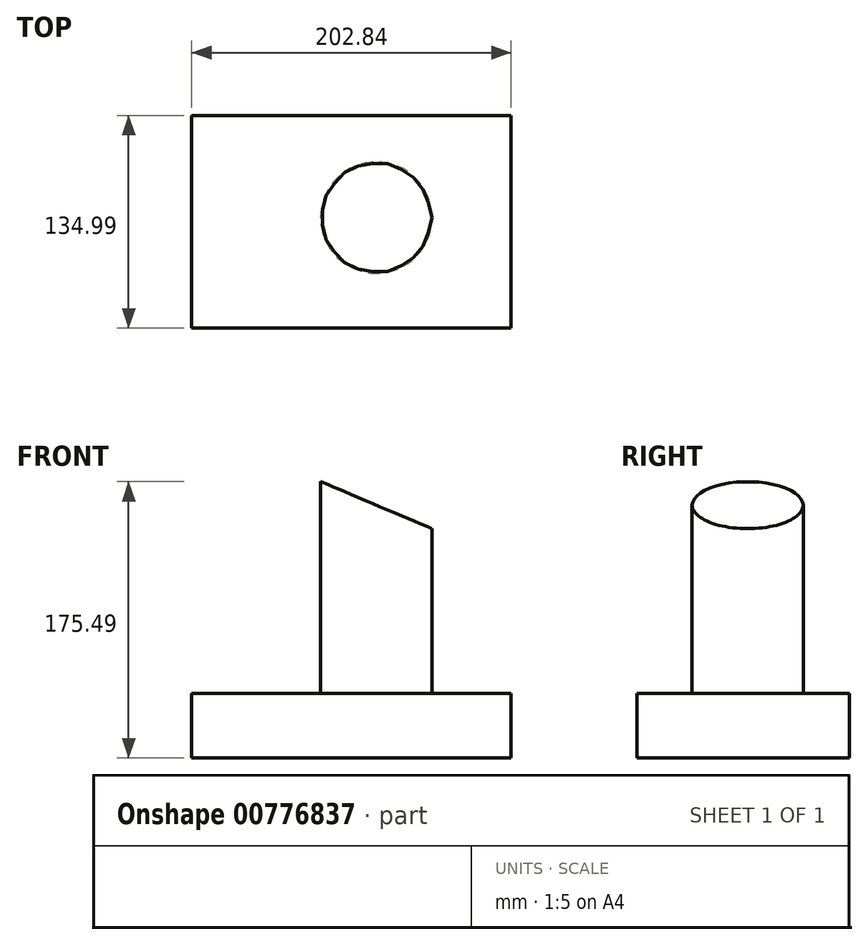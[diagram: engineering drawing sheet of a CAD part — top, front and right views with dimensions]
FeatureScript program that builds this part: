
annotation { "Feature Type Name" : "Feature", "Feature Type Description" : "" }
export const myFeature = defineFeature(function(context is Context, id is Id, definition is map)
    precondition{}
    {
        {
            var Q0;
            Q0=qCreatedBy(makeId("Top.planeOp"),FACE);
            var sketch = newSketch(context, id + "F0", { "sketchPlane" : qUnion([Q0])});
            skLineSegment(sketch, "E0.bottom", {"start": v(46.58, 55.38) * mm, "end": v(-156.26, 55.38) * mm});
            skLineSegment(sketch, "E0.top", {"start": v(46.58, -79.6) * mm, "end": v(-156.26, -79.6) * mm});
            skLineSegment(sketch, "E0.left", {"start": v(46.58, 55.38) * mm, "end": v(46.58, -79.6) * mm});
            skLineSegment(sketch, "E0.right", {"start": v(-156.26, 55.38) * mm, "end": v(-156.26, -79.6) * mm});
            skSolve(sketch);
        }
        {
            var Q0;
            Q0=makeQuery(id+"F0.imprint","IMPRINT",FACE,{"disambiguationData":[TD([[makeQuery(id+"F0.imprint","IMPRINT",EDGE,{"derivedFrom":sQuery(id+"F0.wireOp",EDGE,"E0.bottom")}),1.0]])]});
            extrude(context, id + "F1", {"entities" : qUnion([Q0]), "depth" : 40.9 * mm, "offsetDistance" : 25.4 * mm});
        }
        {
            var Q0;
            Q0=makeQuery(id+"F1.opExtrude","CAP_FACE",FACE,{"disambiguationData":[OSD([sQuery(id+"F0.wireOp",EDGE,"E0.bottom"),sQuery(id+"F0.wireOp",EDGE,"E0.top"),sQuery(id+"F0.wireOp",EDGE,"E0.left"),sQuery(id+"F0.wireOp",EDGE,"E0.right")])],"isStart":false});
            var sketch = newSketch(context, id + "F2", { "sketchPlane" : qUnion([Q0])});
            skCircle(sketch, "E1", {"center": v(-39.07, -9.41) * mm, "radius": 35.28 * mm});
            skSolve(sketch);
        }
        {
            var Q0;
            Q0=makeQuery(id+"F2.imprint","IMPRINT",FACE,{"disambiguationData":[TD([[makeQuery(id+"F2.imprint","IMPRINT",EDGE,{"derivedFrom":sQuery(id+"F2.wireOp",EDGE,"E1")}),1.0]])]});
            extrude(context, id + "F3", {"entities" : qUnion([Q0]), "operationType" : NewBodyOperationType.ADD, "depth" : 134.62 * mm, "offsetDistance" : 25.4 * mm});
        }
        {
            var Q0;
            Q0=qCreatedBy(makeId("Front.planeOp"),FACE);
            var sketch = newSketch(context, id + "F4", { "sketchPlane" : qUnion([Q0])});
            skLineSegment(sketch, "E2", {"start": v(-104.44, 188.22) * mm, "end": v(38.17, 127.85) * mm});
            skLineSegment(sketch, "E3", {"start": v(38.17, 193.45) * mm, "end": v(-104.44, 188.22) * mm});
            skLineSegment(sketch, "E4", {"start": v(38.17, 193.45) * mm, "end": v(38.17, 127.85) * mm});
            skSolve(sketch);
        }
        {
            var Q0;
            Q0 = qSketchRegion(id + "F4", true);
            extrude(context, id + "F5", {"entities" : qUnion([Q0]), "operationType" : NewBodyOperationType.REMOVE, "endBound" : BoundingType.SYMMETRIC, "depth" : 192.02 * mm, "offsetDistance" : 25.4 * mm});
        }
    });
